# Revit family: f86dde23-1ac0-43b9-aa82-2ef082b00fc8_TSA325NT_revit_template_model_3d_rfa
name_source: partatom
category: Doors
units: mm (PartAtom-declared; Revit-internal decimal feet)

## family parameters
Always vertical = Yes
Cut with Voids When Loaded = Yes
Host = Wall
OmniClass Number = 23.30.10.17.21
OmniClass Title = Revolving Doors
Room Calculation Point = No
Shared = No

## types (4) — shared parameters
Analytic Construction = <None>
Define Thermal Properties by = Schematic Type
FP_Altura_de_puerta = 2400 mm
FP_Altura_del_motor_empotrado_de_suelo = 278 mm  [stored 0.912073 ft]
FP_Ancho_de_hoja = 930 mm  [stored 3.05118 ft]
FP_Ancho_del_motor_empotrado_de_suelo = 780 mm  [stored 2.55906 ft]
FP_Compensación_medida_altura_de_canopy = 200 mm  [stored 0.656168 ft]
FP_Diámetro_exterior_de_puerta = 2000 mm  [stored 6.56168 ft]
FP_Longitud_del_motor_empotrado_de_suelo = 1470 mm
FP_Material_Anillo_de_suelo = Stainless_steel
FP_Material_de_recubrimiento_de_suelo = Rubber Black
FP_Material_de_relleno_de_la_hoja = Glass
FP_Material_del_marco = Aluminium
FP_Posición_de_la_flecha = 620 mm  [stored 2.03412 ft]
FP_Radio_externo = 1000 mm  [stored 3.28084 ft]
FP_Radio_interno = 960 mm  [stored 3.14961 ft]
Function = Exterior
Manufacturer = GEZE GmbH
Operation = REVOLVING
SP_Altura_paso_libre = 3000
SP_Aro_de_suelo = Si
SP_Conformidad_estándar = DIN 18650, EN 16005
SP_GEZE_Documentos = https://pic.geze.com
SP_Manejo_totalmente_automático = Si
SP_Para_sistemas_de_puerta_de_3_hojas = Si
SP_Para_sistemas_de_puerta_de_4_hojas = Si
SP_Pulsador_para_discapacitados = Si
SP_Revestimiento_del_suelo = Entrance mat, Entrance mat according to customer wishes
SP_Tiradores_de_la_puerta_horizontales_o_verticales = Si
Thickness = 30 mm  [stored 0.0984252 ft]
URL = https://www.geze.com
Wall Closure = By host
Width = 2000 mm  [stored 6.56168 ft]

## per-type parameters (varying)
- TSA 325 NT (automatic): Description=Automatic revolving door drive for three- or four-leaf doors with large area of application; FP_3_hojas=No; FP_4_hojas=Yes; FP_Altura_de_canopy=200 mm  [stored 0.656168 ft]; FP_Altura_de_marco_RC2=0 mm  [stored 0 ft]; FP_Altura_de_paso=2200 mm; FP_Ancho_de_marco_RC2=0 mm  [stored 0 ft]; FP_Ancho_de_paso_CAL=1274 mm; FP_Ancho_perfil_vertical_interior_hoja_móvil=35 mm  [stored 0.114829 ft]; FP_Detalles_de_salida_2D=No; FP_Diámetro_de_puerta_con_cierre_nocturno=2000 mm  [stored 6.56168 ft]; FP_Eje_central=Yes; FP_Material _del_Canopy=Aluminium; FP_Motor_en_suelo=No; FP_Puerta_con_cierre_nocturno=No; FP_Puerta_con_cierre_nocturno_exterior=Yes; FP_Puerta_con_cierre_nocturno_interior=No; FP_Puerta_sin_cierre_nocturno=Yes; FP_Techo_de_cristal=No; FP_Ángulo=45.00°; GEZEIDBIM=4484; Height=2200 mm; Model=TSA 325 NT; Rough Height=2400 mm; Rough Width=2000 mm  [stored 6.56168 ft]; SP_Altura_de_la_cubierta_mín=200; SP_Automatismo_de_pavimento=Si; SP_Bloqueo=Manualmente, Barra, electromecánica; SP_Con_automatismo_de_posicionamiento_opcional=Si; SP_Con_reductor_de_velocidad_opcional=Si; SP_Cortina_de_aire=Cortina de aire eléctrica, Cortina de aire de agua caliente, en función de la version constructiva del techo; SP_Disposición_cierre_nocturno=Interior, Exterior; SP_Diámetro_interior_máx=3600; SP_Diámetro_interior_mín=1800; SP_Función_Break_out_BO=No; SP_Función_Servo=Si; SP_Idoneidad_para_puertas_de_rutas_de_evacuación_y_emergencia=No; SP_Iluminación=en la variante con techo; SP_Manejo_manual=Si; SP_Modelo_cierre_nocturno=VSG de 10 mm, Vidrio ISO de 22 mm, panel con relleno de 22 mm, vidrios especiales bajo solicitud; SP_Tipo_cierre_nocturno=Manualmente, Automático; SP_Versiones_constructivas_del_techo=Techo guardapolvo con cubierta de madera, cobertor de chapa óptico, techo impermeable con vierteaguas; SP_Versión_partes_laterales=VSG de 10 mm, panel con relleno de 22 mm, panel liso de 34 mm, vidrios especiales bajo solicitud
- TSA 325 NT BO: Description=Automatic revolving door system for escape and rescue routes with break-out function; FP_3_hojas=Yes; FP_4_hojas=No; FP_Altura_de_canopy=200 mm  [stored 0.656168 ft]; FP_Altura_de_marco_RC2=0 mm  [stored 0 ft]; FP_Altura_de_paso=2200 mm; FP_Ancho_de_marco_RC2=0 mm  [stored 0 ft]; FP_Ancho_de_paso_CAL=890 mm  [stored 2.91995 ft]; FP_Ancho_perfil_vertical_interior_hoja_móvil=35 mm  [stored 0.114829 ft]; FP_Detalles_de_salida_2D=Yes; FP_Diámetro_de_puerta_con_cierre_nocturno=2000 mm  [stored 6.56168 ft]; FP_Eje_central=Yes; FP_Material _del_Canopy=Aluminium; FP_Motor_en_suelo=No; FP_Puerta_con_cierre_nocturno=No; FP_Puerta_con_cierre_nocturno_exterior=Yes; FP_Puerta_con_cierre_nocturno_interior=No; FP_Puerta_sin_cierre_nocturno=Yes; FP_Techo_de_cristal=No; FP_Ángulo=60.00°; GEZEIDBIM=31026; Height=2200 mm; Model=TSA 325 NT BO; Rough Height=2400 mm; Rough Width=2000 mm  [stored 6.56168 ft]; SP_Altura_de_la_cubierta_mín=200; SP_Automatismo_de_pavimento=No; SP_Bloqueo=Manualmente, Barra, electromecánica; SP_Con_automatismo_de_posicionamiento_opcional=No; SP_Con_reductor_de_velocidad_opcional=No; SP_Cortina_de_aire=Cortina de aire eléctrica, Cortina de aire de agua caliente, en función de la version constructiva del techo; SP_Disposición_cierre_nocturno=Interior, Exterior; SP_Diámetro_interior_máx=3600; SP_Diámetro_interior_mín=1800; SP_Función_Break_out_BO=Si; SP_Función_Servo=No; SP_Idoneidad_para_puertas_de_rutas_de_evacuación_y_emergencia=Si; SP_Iluminación=en la variante con techo; SP_Manejo_manual=No; SP_Modelo_cierre_nocturno=VSG de 10 mm, Vidrio ISO de 22 mm, panel con relleno de 22 mm, vidrios especiales bajo solicitud; SP_Tipo_cierre_nocturno=Manualmente, Automático; SP_Versiones_constructivas_del_techo=Techo guardapolvo con cubierta de madera, cobertor de chapa óptico, techo impermeable con vierteaguas; SP_Versión_partes_laterales=VSG de 10 mm, panel con relleno de 22 mm, panel liso de 34 mm, vidrios especiales bajo solicitud
- TSA 325 NT RC2: Description=Automatic GEZE revolving door with RC2 and night time closing; FP_3_hojas=Yes; FP_4_hojas=No; FP_Altura_de_canopy=200 mm  [stored 0.656168 ft]; FP_Altura_de_marco_RC2=128 mm  [stored 0.419948 ft]; FP_Altura_de_paso=2200 mm; FP_Ancho_de_marco_RC2=154 mm; FP_Ancho_de_paso_CAL=890 mm  [stored 2.91995 ft]; FP_Ancho_perfil_vertical_interior_hoja_móvil=35 mm  [stored 0.114829 ft]; FP_Detalles_de_salida_2D=No; FP_Diámetro_de_puerta_con_cierre_nocturno=2105 mm  [stored 6.90617 ft]; FP_Eje_central=Yes; FP_Material _del_Canopy=Aluminium; FP_Motor_en_suelo=No; FP_Puerta_con_cierre_nocturno=Yes; FP_Puerta_con_cierre_nocturno_exterior=No; FP_Puerta_con_cierre_nocturno_interior=Yes; FP_Puerta_sin_cierre_nocturno=No; FP_Techo_de_cristal=No; FP_Ángulo=60.00°; GEZEIDBIM=37707; Height=2200 mm; Model=TSA 325 NT RC2; Rough Height=2528 mm; Rough Width=2308 mm; SP_Altura_de_la_cubierta_mín=200; SP_Automatismo_de_pavimento=No; SP_Bloqueo=Manualmente, Barra, electromecánica; SP_Con_automatismo_de_posicionamiento_opcional=Si; SP_Con_reductor_de_velocidad_opcional=Si; SP_Cortina_de_aire=Cortina de aire eléctrica, Cortina de aire de agua caliente, en función de la version constructiva del techo; SP_Disposición_cierre_nocturno=Interior; SP_Diámetro_interior_máx=3400; SP_Diámetro_interior_mín=2500; SP_Función_Break_out_BO=No; SP_Función_Servo=Si; SP_Idoneidad_para_puertas_de_rutas_de_evacuación_y_emergencia=No; SP_Iluminación=en la variante con techo; SP_Manejo_manual=Si; SP_Modelo_cierre_nocturno=VSG de 10 mm; SP_Tipo_cierre_nocturno=Automático; SP_Versiones_constructivas_del_techo=cobertor de chapa óptico, techo impermeable con vierteaguas; SP_Versión_partes_laterales=VSG de 10 mm
- TSA 325 NT GG: Description=Automatic revolving door system for the realization of all-glass solutions; FP_3_hojas=Yes; FP_4_hojas=No; FP_Altura_de_canopy=20 mm  [stored 0.0656168 ft]; FP_Altura_de_marco_RC2=0 mm  [stored 0 ft]; FP_Altura_de_paso=2380 mm  [stored 7.8084 ft]; FP_Ancho_de_marco_RC2=0 mm  [stored 0 ft]; FP_Ancho_de_paso_CAL=890 mm  [stored 2.91995 ft]; FP_Ancho_perfil_vertical_interior_hoja_móvil=1 mm  [stored 0.00328084 ft]; FP_Detalles_de_salida_2D=No; FP_Diámetro_de_puerta_con_cierre_nocturno=2000 mm  [stored 6.56168 ft]; FP_Eje_central=No; FP_Material _del_Canopy=Glass; FP_Motor_en_suelo=Yes; FP_Puerta_con_cierre_nocturno=No; FP_Puerta_con_cierre_nocturno_exterior=Yes; FP_Puerta_con_cierre_nocturno_interior=No; FP_Puerta_sin_cierre_nocturno=Yes; FP_Techo_de_cristal=Yes; FP_Ángulo=60.00°; GEZEIDBIM=31025; Height=2380 mm  [stored 7.8084 ft]; Model=TSA 325 NT GG; Rough Height=2400 mm; Rough Width=2000 mm  [stored 6.56168 ft]; SP_Altura_de_la_cubierta_mín=17; SP_Automatismo_de_pavimento=Si; SP_Bloqueo=Manualmente; SP_Con_automatismo_de_posicionamiento_opcional=Si; SP_Con_reductor_de_velocidad_opcional=Si; SP_Cortina_de_aire=bajo pedido; SP_Disposición_cierre_nocturno=Exterior; SP_Diámetro_interior_máx=3000; SP_Diámetro_interior_mín=1800; SP_Función_Break_out_BO=No; SP_Función_Servo=Si; SP_Idoneidad_para_puertas_de_rutas_de_evacuación_y_emergencia=No; SP_Iluminación=en el techo de vidrio no es posible; SP_Manejo_manual=Si; SP_Modelo_cierre_nocturno=VSG de 10 mm; SP_Tipo_cierre_nocturno=Manualmente; SP_Versiones_constructivas_del_techo=techo de vidrio; SP_Versión_partes_laterales=GG de 16 mm, vidrios especiales bajo solicitud

note: column(s) folded — value = type name in every type: Nombre_del_producto

note: [stored X ft] marks values corroborated as IEEE doubles in the binary element streams (Revit-internal decimal feet)
